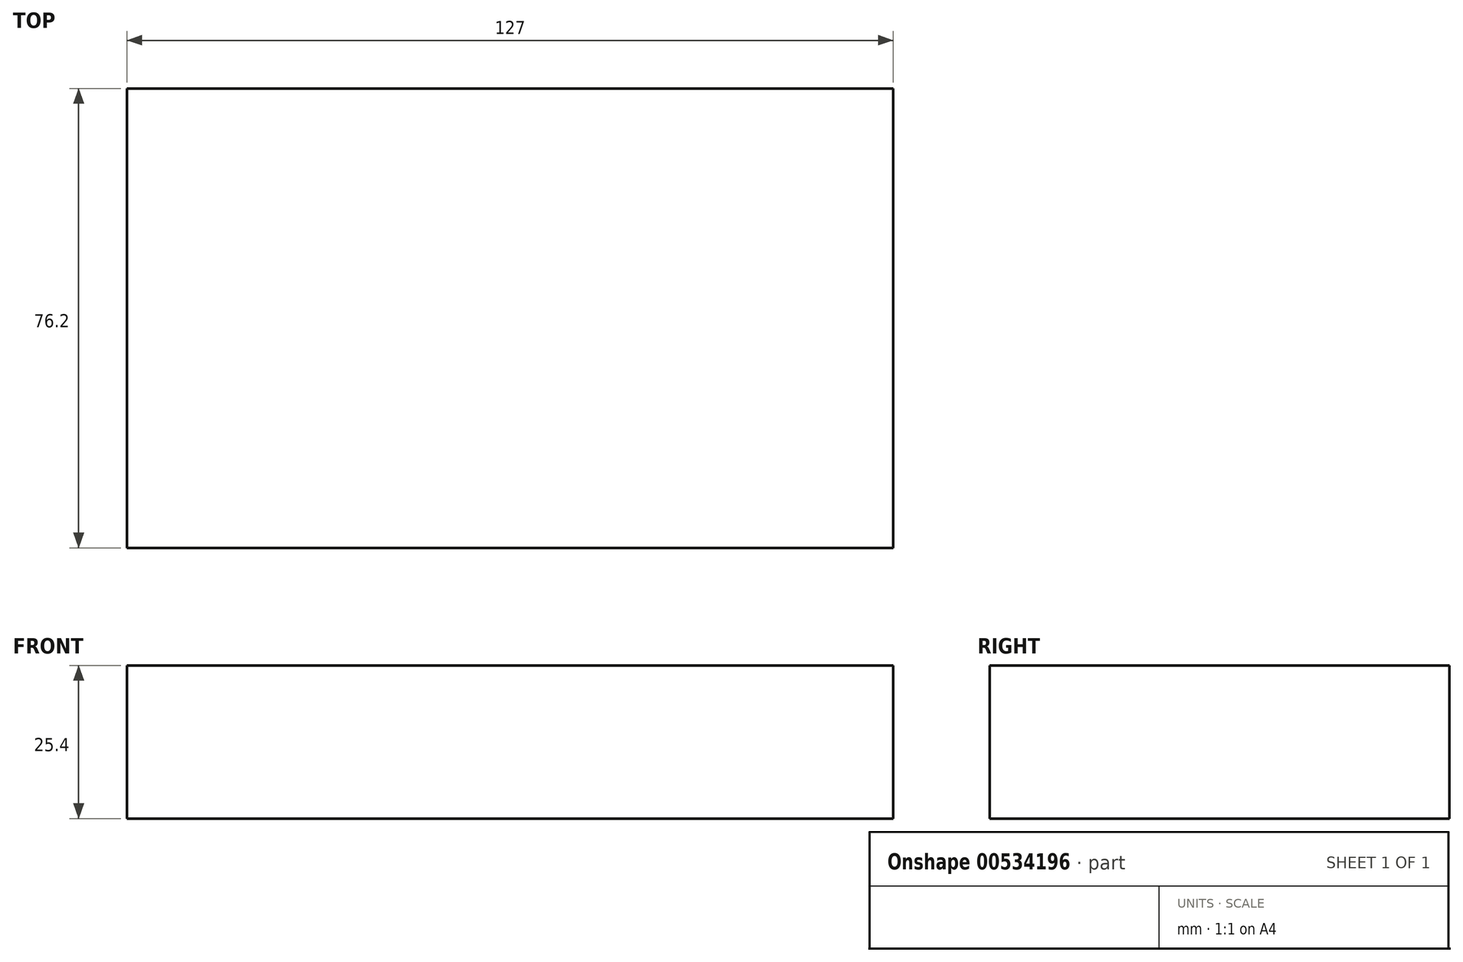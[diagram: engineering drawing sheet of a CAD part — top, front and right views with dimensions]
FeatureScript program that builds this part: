
annotation { "Feature Type Name" : "Feature", "Feature Type Description" : "" }
export const myFeature = defineFeature(function(context is Context, id is Id, definition is map)
    precondition{}
    {
        {
            var Q0;
            Q0=qCreatedBy(makeId("Top.planeOp"),FACE);
            var sketch = newSketch(context, id + "F0", { "sketchPlane" : qUnion([Q0])});
            skLineSegment(sketch, "E0.bottom", {"start": v(-63.5, 38.1) * mm, "end": v(63.5, 38.1) * mm});
            skLineSegment(sketch, "E0.top", {"start": v(-63.5, -38.1) * mm, "end": v(63.5, -38.1) * mm});
            skLineSegment(sketch, "E0.left", {"start": v(-63.5, 38.1) * mm, "end": v(-63.5, -38.1) * mm});
            skLineSegment(sketch, "E0.right", {"start": v(63.5, 38.1) * mm, "end": v(63.5, -38.1) * mm});
            skPoint(sketch, "E0.middle", {"position": v(0, 0) * mm});
            skSolve(sketch);
        }
        {
            var Q0;
            Q0 = qSketchRegion(id + "F0", true);
            extrude(context, id + "F1", {"entities" : qUnion([Q0]), "depth" : 25.4 * mm});
        }
    });
